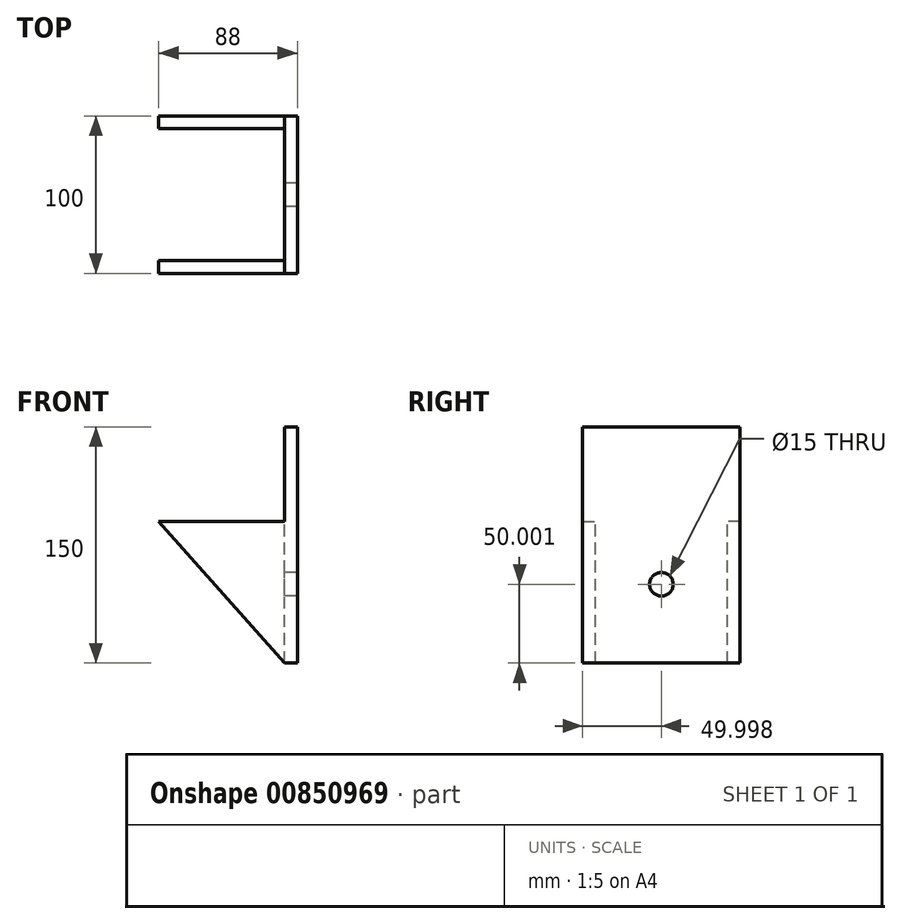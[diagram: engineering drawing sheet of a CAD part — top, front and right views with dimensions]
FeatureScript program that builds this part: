
annotation { "Feature Type Name" : "Feature", "Feature Type Description" : "" }
export const myFeature = defineFeature(function(context is Context, id is Id, definition is map)
    precondition{}
    {
        {
            var Q0;
            Q0=qCreatedBy(makeId("Right.planeOp"),FACE);
            var sketch = newSketch(context, id + "F0", { "sketchPlane" : qUnion([Q0])});
            skLineSegment(sketch, "E0.bottom", {"start": v(-54.85, 95) * mm, "end": v(45.15, 95) * mm});
            skLineSegment(sketch, "E0.top", {"start": v(-54.85, -55) * mm, "end": v(45.15, -55) * mm});
            skLineSegment(sketch, "E0.left", {"start": v(-54.85, 95) * mm, "end": v(-54.85, -55) * mm});
            skLineSegment(sketch, "E0.right", {"start": v(45.15, 95) * mm, "end": v(45.15, -55) * mm});
            skCircle(sketch, "E1", {"center": v(-4.85, -5) * mm, "radius": 7.5 * mm});
            skSolve(sketch);
        }
        {
            var Q0;
            Q0 = qSketchRegion(id + "F0", true);
            extrude(context, id + "F1", {"entities" : qUnion([Q0]), "depth" : 8 * mm, "offsetDistance" : 25 * mm});
        }
        {
            var Q0;
            Q0=makeQuery(id+"F1.opExtrude","CAP_FACE",FACE,{"disambiguationData":[OSD([sQuery(id+"F0.wireOp",EDGE,"E0.bottom"),sQuery(id+"F0.wireOp",EDGE,"E0.top"),sQuery(id+"F0.wireOp",EDGE,"E0.left"),sQuery(id+"F0.wireOp",EDGE,"E0.right"),sQuery(id+"F0.wireOp",EDGE,"E1")])],"isStart":true});
            var sketch = newSketch(context, id + "F2", { "sketchPlane" : qUnion([Q0])});
            skLineSegment(sketch, "E2.bottom", {"start": v(54.85, -55) * mm, "end": v(46.85, -55) * mm});
            skLineSegment(sketch, "E2.top", {"start": v(54.85, 35) * mm, "end": v(46.85, 35) * mm});
            skLineSegment(sketch, "E2.left", {"start": v(54.85, -55) * mm, "end": v(54.85, 35) * mm});
            skLineSegment(sketch, "E2.right", {"start": v(46.85, -55) * mm, "end": v(46.85, 35) * mm});
            skLineSegment(sketch, "E3.bottom", {"start": v(-45.15, -55) * mm, "end": v(-37.15, -55) * mm});
            skLineSegment(sketch, "E3.top", {"start": v(-45.15, 35) * mm, "end": v(-37.15, 35) * mm});
            skLineSegment(sketch, "E3.left", {"start": v(-45.15, -55) * mm, "end": v(-45.15, 35) * mm});
            skLineSegment(sketch, "E3.right", {"start": v(-37.15, -55) * mm, "end": v(-37.15, 35) * mm});
            skSolve(sketch);
        }
        {
            var Q0;
            Q0 = qSketchRegion(id + "F2", true);
            extrude(context, id + "F3", {"entities" : qUnion([Q0]), "operationType" : NewBodyOperationType.ADD, "depth" : 80 * mm, "offsetDistance" : 25 * mm});
        }
        {
            var Q0;
            Q0=makeQuery(id+"F3.boolean.opBoolean","MERGE",FACE,{"derivedFrom":[makeQuery(id+"F1.opExtrude","SWEPT_FACE",FACE,{"disambiguationData":[OSD([sQuery(id+"F0.wireOp",EDGE,"E0.right")])]}),makeQuery(id+"F3.opExtrude","SWEPT_FACE",FACE,{"disambiguationData":[OSD([sQuery(id+"F2.wireOp",EDGE,"E3.left")])]})]});
            var sketch = newSketch(context, id + "F4", { "sketchPlane" : qUnion([Q0])});
            skLineSegment(sketch, "E4", {"start": v(80, 35) * mm, "end": v(0, -55) * mm});
            skLineSegment(sketch, "E5", {"start": v(0, -55) * mm, "end": v(80, -55) * mm});
            skLineSegment(sketch, "E6", {"start": v(80, -55) * mm, "end": v(80, 35) * mm});
            skSolve(sketch);
        }
        {
            var Q0;
            Q0 = qSketchRegion(id + "F4", true);
            extrude(context, id + "F5", {"entities" : qUnion([Q0]), "operationType" : NewBodyOperationType.REMOVE, "endBound" : BoundingType.THROUGH_ALL, "oppositeDirection" : true, "depth" : 25 * mm, "offsetDistance" : 25 * mm});
        }
    });
